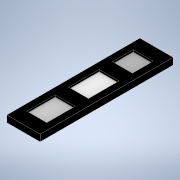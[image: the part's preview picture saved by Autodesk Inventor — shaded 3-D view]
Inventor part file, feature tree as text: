
AUTODESK INVENTOR PART (.ipt)
format: ipt  version: 2021 (Build 250183000, 183)  size: 124,928 bytes
history: native  units: mm
features: extrude x2, sketch x2
ambient origin geometry x8: Origin, YZ Plane, XZ Plane, XY Plane, X Axis, Y Axis, Z Axis, Center Point
bodies: Solid1 (feature_tree)
feature tree (4):
  extrude  "Extrusion1"  Depth=200.0mm
  extrude  "Extrusion2"  Depth=20.0mm
  sketch  "Sketch1"  dims[d0=50.0mm d1=200.0mm]
  sketch  "Sketch2"  dims[d2=10.0mm d3=0.0mm d4=20.0mm d5=20.0mm d6=20.0mm d7=20.0mm d8=10.0mm d9=10.0mm d10=10.0mm d11=10.0mm d12=3.0mm d13=0.0mm]
